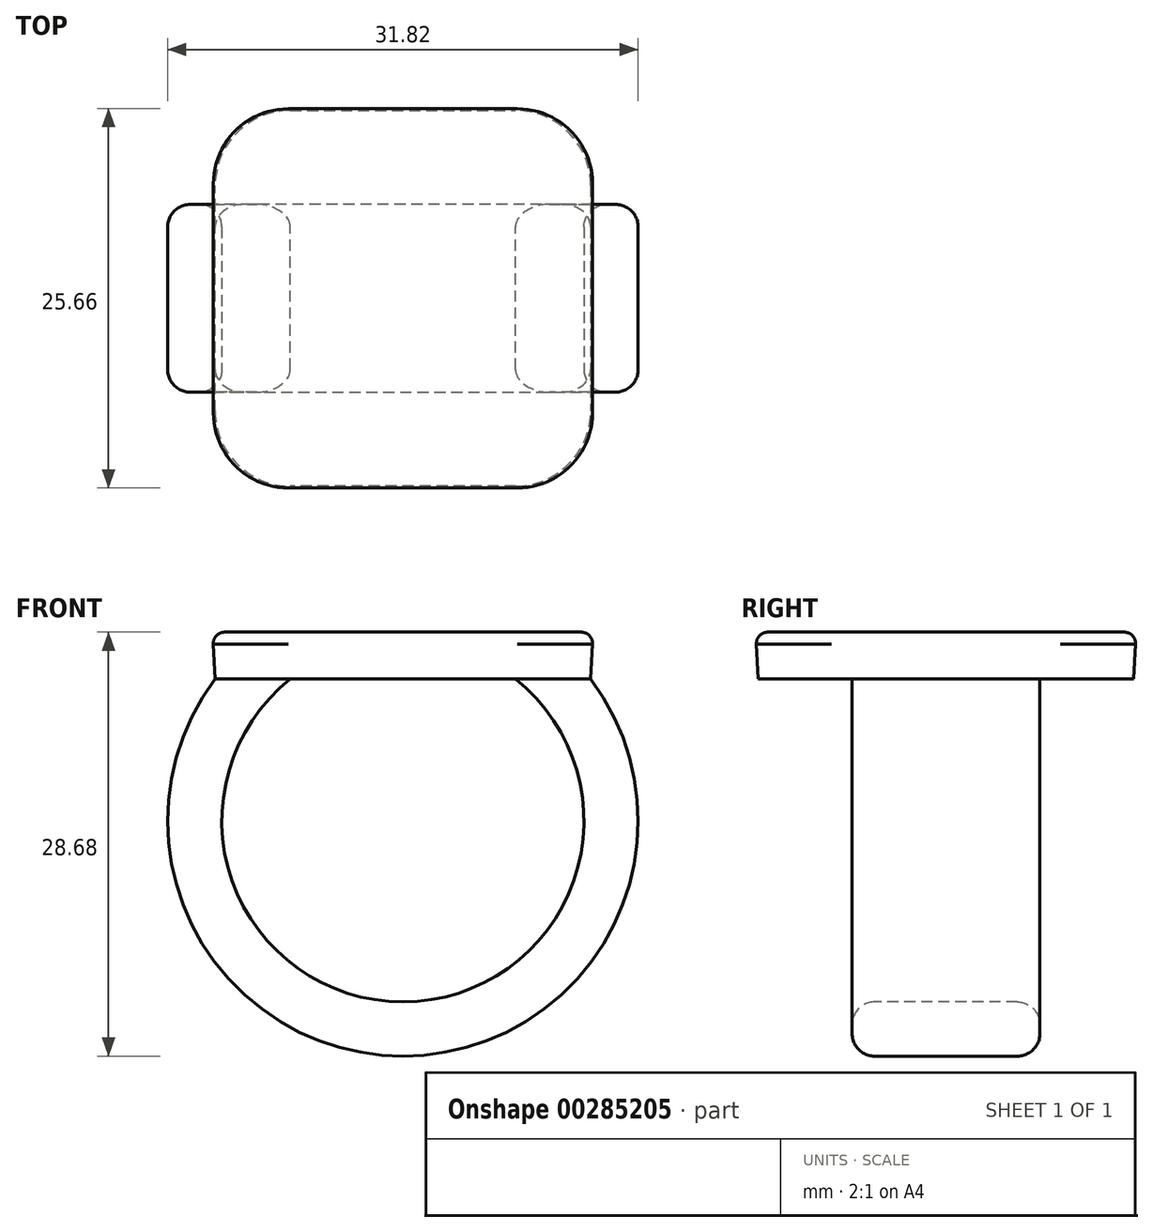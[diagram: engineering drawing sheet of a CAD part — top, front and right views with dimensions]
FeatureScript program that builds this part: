
annotation { "Feature Type Name" : "Feature", "Feature Type Description" : "" }
export const myFeature = defineFeature(function(context is Context, id is Id, definition is map)
    precondition{}
    {
        {
            var Q0;
            Q0=qCreatedBy(makeId("Top.planeOp"),FACE);
            var sketch = newSketch(context, id + "F0", { "sketchPlane" : qUnion([Q0])});
            skLineSegment(sketch, "E0.bottom", {"start": v(12.7, 12.7) * mm, "end": v(-12.7, 12.7) * mm});
            skLineSegment(sketch, "E0.top", {"start": v(12.7, -12.7) * mm, "end": v(-12.7, -12.7) * mm});
            skLineSegment(sketch, "E0.left", {"start": v(12.7, 12.7) * mm, "end": v(12.7, -12.7) * mm});
            skLineSegment(sketch, "E0.right", {"start": v(-12.7, 12.7) * mm, "end": v(-12.7, -12.7) * mm});
            skPoint(sketch, "E0.middle", {"position": v(0, 0) * mm});
            skSolve(sketch);
        }
        {
            var Q0;
            Q0 = qSketchRegion(id + "F0", true);
            extrude(context, id + "F1", {"entities" : qUnion([Q0]), "depth" : 3.17 * mm, "hasDraft" : true, "draftAngle" : 3 * degree});
        }
        {
            var Q0;
            Q0=qCreatedBy(makeId("Front.planeOp"),FACE);
            var sketch = newSketch(context, id + "F2", { "sketchPlane" : qUnion([Q0])});
            skArc(sketch, "E1", {"start": v(-10.16, 0) * mm, "mid": v(0, -23.56) * mm, "end": v(10.16, 0) * mm});
            skSolve(sketch);
        }
        {
            var Q0;
            Q0=makeQuery(id+"F1.opExtrude","CAP_FACE",FACE,{"disambiguationData":[OSD([sQuery(id+"F0.wireOp",EDGE,"E0.bottom"),sQuery(id+"F0.wireOp",EDGE,"E0.top"),sQuery(id+"F0.wireOp",EDGE,"E0.left"),sQuery(id+"F0.wireOp",EDGE,"E0.right")])],"isStart":true});
            var sketch = newSketch(context, id + "F3", { "sketchPlane" : qUnion([Q0])});
            skLineSegment(sketch, "E2.bottom", {"start": v(-7.62, 6.35) * mm, "end": v(-12.7, 6.35) * mm});
            skLineSegment(sketch, "E2.top", {"start": v(-7.62, -6.35) * mm, "end": v(-12.7, -6.35) * mm});
            skLineSegment(sketch, "E2.left", {"start": v(-7.62, 6.35) * mm, "end": v(-7.62, -6.35) * mm});
            skLineSegment(sketch, "E2.right", {"start": v(-12.7, 6.35) * mm, "end": v(-12.7, -6.35) * mm});
            skPoint(sketch, "E2.middle", {"position": v(-10.16, 0) * mm});
            skSolve(sketch);
        }
        {
            var Q0;
            Q0 = qSketchRegion(id + "F3", true);
            var Q1;
            Q1 = qConstructionFilter(qBodyType(qCreatedBy(id + "F2" ,EDGE), BodyType.WIRE), ConstructionObject.NO);
            sweep(context, id + "F4", {"operationType" : NewBodyOperationType.ADD, "profiles" : qUnion([Q0]), "path" : qUnion([Q1])});
        }
        {
            var Q0;
            Q0=qCreatedBy(makeId("Front.planeOp"),FACE);
            var sketch = newSketch(context, id + "F5", { "sketchPlane" : qUnion([Q0])});
            skLineSegment(sketch, "E3.0", {"start": v(10.16, 0) * mm, "end": v(7.62, 0) * mm});
            skLineSegment(sketch, "E3.1", {"start": v(10.01, -2.54) * mm, "end": v(10.16, 0) * mm});
            skArc(sketch, "E3.2", {"start": v(10.01, -2.54) * mm, "mid": v(8.9, -1.18) * mm, "end": v(7.62, 0) * mm});
            skLineSegment(sketch, "E4.trimOffspring", {"start": v(-7.62, 0) * mm, "end": v(-12.7, 0) * mm});
            skPoint(sketch, "E5.orphan", {"position": v(12.7, 0) * mm});
            skSolve(sketch);
        }
        {
            var Q0;
            Q0 = qSketchRegion(id + "F5", true);
            var Q1;
            Q1=makeQuery(id+"F4.opSweep","SWEPT_FACE",FACE,{"disambiguationData":[OSD([sQuery(id+"F2.wireOp",EDGE,"E1"),sQuery(id+"F3.wireOp",EDGE,"E2.bottom")])]});
            var Q2;
            Q2=makeQuery(id+"F4.opSweep","SWEPT_FACE",FACE,{"disambiguationData":[OSD([sQuery(id+"F2.wireOp",EDGE,"E1"),sQuery(id+"F3.wireOp",EDGE,"E2.top")])]});
            extrude(context, id + "F6", {"entities" : qUnion([Q0]), "operationType" : NewBodyOperationType.ADD, "endBound" : BoundingType.UP_TO_SURFACE, "endBoundEntityFace" : qUnion([Q1]), "depth" : 25.4 * mm, "hasSecondDirection" : true, "secondDirectionBound" : SecondDirectionBoundingType.UP_TO_SURFACE, "secondDirectionOppositeDirection" : true, "secondDirectionBoundEntityFace" : qUnion([Q2]), "secondDirectionDepth" : 25.4 * mm});
        }
        {
            var Q0;
            Q0=makeQuery(id+"F1.opExtrude","SWEPT_EDGE",EDGE,{"disambiguationData":[OSD([sQuery(id+"F0.wireOp",EDGE,"E0.top"),sQuery(id+"F0.wireOp",EDGE,"E0.right")])]});
            var Q1;
            Q1=makeQuery(id+"F1.opExtrude","SWEPT_EDGE",EDGE,{"disambiguationData":[OSD([sQuery(id+"F0.wireOp",EDGE,"E0.bottom"),sQuery(id+"F0.wireOp",EDGE,"E0.right")])]});
            var Q2;
            Q2=makeQuery(id+"F1.opExtrude","SWEPT_EDGE",EDGE,{"disambiguationData":[OSD([sQuery(id+"F0.wireOp",EDGE,"E0.top"),sQuery(id+"F0.wireOp",EDGE,"E0.left")])]});
            var Q3;
            Q3=makeQuery(id+"F1.opExtrude","SWEPT_EDGE",EDGE,{"disambiguationData":[OSD([sQuery(id+"F0.wireOp",EDGE,"E0.bottom"),sQuery(id+"F0.wireOp",EDGE,"E0.left")])]});
            fillet(context, id + "F7", {"entities" : qUnion([Q0, Q1, Q2, Q3]), "radius" : 5.08 * mm, "tangentPropagation" : true, "allowEdgeOverflow" : false});
        }
        {
            var Q0;
            Q0=makeQuery(id+"F4.opSweep","SWEPT_EDGE",EDGE,{"disambiguationData":[OSD([sQuery(id+"F0.wireOp",EDGE,"E0.right"),sQuery(id+"F2.wireOp",EDGE,"E1"),sQuery(id+"F3.wireOp",EDGE,"E2.bottom"),sQuery(id+"F3.wireOp",EDGE,"E2.right")])]});
            var Q1;
            {var subQ0=sQuery(id+"F3.wireOp",EDGE,"E2.top");var subQ1=sQuery(id+"F2.wireOp",EDGE,"E1");Q1=makeQuery(id+"F6.boolean.opBoolean","MERGE",EDGE,{"derivedFrom":[makeQuery(id+"F4.opSweep","SWEPT_EDGE",EDGE,{"disambiguationData":[OSD([subQ1,subQ0,sQuery(id+"F3.wireOp",EDGE,"E2.left")])]}),makeQuery(id+"F6.opExtrude","TWEAK_EDGE",EDGE,{"derivedFrom":[makeQuery(id+"F4.opSweep","SWEPT_FACE",FACE,{"disambiguationData":[OSD([subQ1,subQ0])]}),makeQuery(id+"F5.imprint","IMPRINT",EDGE,{"derivedFrom":sQuery(id+"F5.wireOp",EDGE,"E3.2")})]})]});}
            var Q2;
            Q2=makeQuery(id+"F4.opSweep","SWEPT_EDGE",EDGE,{"disambiguationData":[OSD([sQuery(id+"F0.wireOp",EDGE,"E0.right"),sQuery(id+"F2.wireOp",EDGE,"E1"),sQuery(id+"F3.wireOp",EDGE,"E2.top"),sQuery(id+"F3.wireOp",EDGE,"E2.right")])]});
            var Q3;
            {var subQ0=sQuery(id+"F3.wireOp",EDGE,"E2.bottom");var subQ1=sQuery(id+"F2.wireOp",EDGE,"E1");Q3=makeQuery(id+"F6.boolean.opBoolean","MERGE",EDGE,{"derivedFrom":[makeQuery(id+"F4.opSweep","SWEPT_EDGE",EDGE,{"disambiguationData":[OSD([subQ1,subQ0,sQuery(id+"F3.wireOp",EDGE,"E2.left")])]}),makeQuery(id+"F6.opExtrude","TWEAK_EDGE",EDGE,{"derivedFrom":[makeQuery(id+"F4.opSweep","SWEPT_FACE",FACE,{"disambiguationData":[OSD([subQ1,subQ0])]}),makeQuery(id+"F5.imprint","IMPRINT",EDGE,{"derivedFrom":sQuery(id+"F5.wireOp",EDGE,"E3.2")})]})]});}
            fillet(context, id + "F8", {"entities" : qUnion([Q0, Q1, Q2, Q3]), "radius" : 1.52 * mm, "tangentPropagation" : true, "allowEdgeOverflow" : false});
        }
        {
            var Q0;
            Q0=makeQuery(id+"F1.opExtrude","CAP_FACE",FACE,{"disambiguationData":[OSD([sQuery(id+"F0.wireOp",EDGE,"E0.bottom"),sQuery(id+"F0.wireOp",EDGE,"E0.top"),sQuery(id+"F0.wireOp",EDGE,"E0.left"),sQuery(id+"F0.wireOp",EDGE,"E0.right")])],"isStart":false});
            fillet(context, id + "F9", {"entities" : qUnion([Q0]), "radius" : 0.76 * mm, "tangentPropagation" : true, "allowEdgeOverflow" : false});
        }
    });
